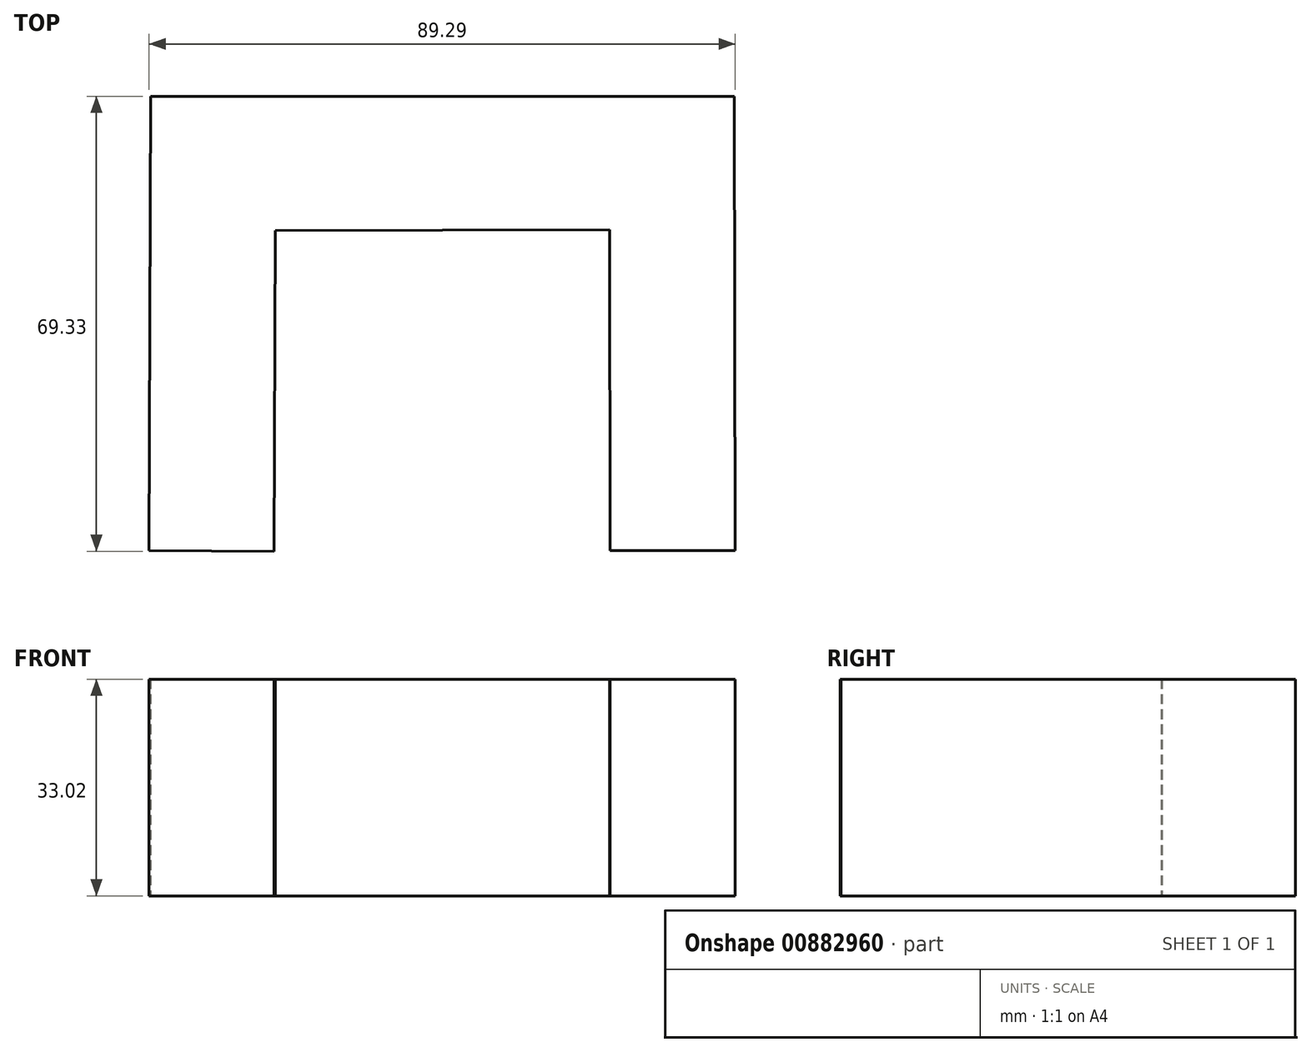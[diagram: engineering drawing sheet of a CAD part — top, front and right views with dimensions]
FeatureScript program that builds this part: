
annotation { "Feature Type Name" : "Feature", "Feature Type Description" : "" }
export const myFeature = defineFeature(function(context is Context, id is Id, definition is map)
    precondition{}
    {
        {
            var Q0;
            Q0=qCreatedBy(makeId("Top.planeOp"),FACE);
            var sketch = newSketch(context, id + "F0", { "sketchPlane" : qUnion([Q0])});
            skLineSegment(sketch, "E0.left", {"start": v(-58.01, -27.87) * mm, "end": v(-57.75, 41.35) * mm});
            skPoint(sketch, "E1.oppositeSnap0", {"position": v(-2.68, 19.74) * mm});
            skLineSegment(sketch, "E2", {"start": v(-58.01, -27.87) * mm, "end": v(-38.96, -27.94) * mm});
            skLineSegment(sketch, "E3", {"start": v(-38.96, -27.94) * mm, "end": v(-38.78, 20.96) * mm});
            skLineSegment(sketch, "E4", {"start": v(-38.78, 20.96) * mm, "end": v(12.14, 21.04) * mm});
            skLineSegment(sketch, "E5", {"start": v(12.14, 21.04) * mm, "end": v(12.23, -27.86) * mm});
            skLineSegment(sketch, "E6", {"start": v(12.23, -27.86) * mm, "end": v(31.28, -27.82) * mm});
            skLineSegment(sketch, "E7", {"start": v(31.28, -27.82) * mm, "end": v(31.15, 41.4) * mm});
            skLineSegment(sketch, "E8", {"start": v(-57.75, 41.35) * mm, "end": v(31.15, 41.4) * mm});
            skSolve(sketch);
        }
        {
            var Q0;
            Q0=makeQuery(id+"F0.imprint","IMPRINT",FACE,{"disambiguationData":[TD([[makeQuery(id+"F0.imprint","IMPRINT",EDGE,{"derivedFrom":sQuery(id+"F0.wireOp",EDGE,"E0.left")}),-1.0]])]});
            extrude(context, id + "F1", {"entities" : qUnion([Q0]), "depth" : 33.02 * mm, "offsetDistance" : 25.4 * mm});
        }
    });
